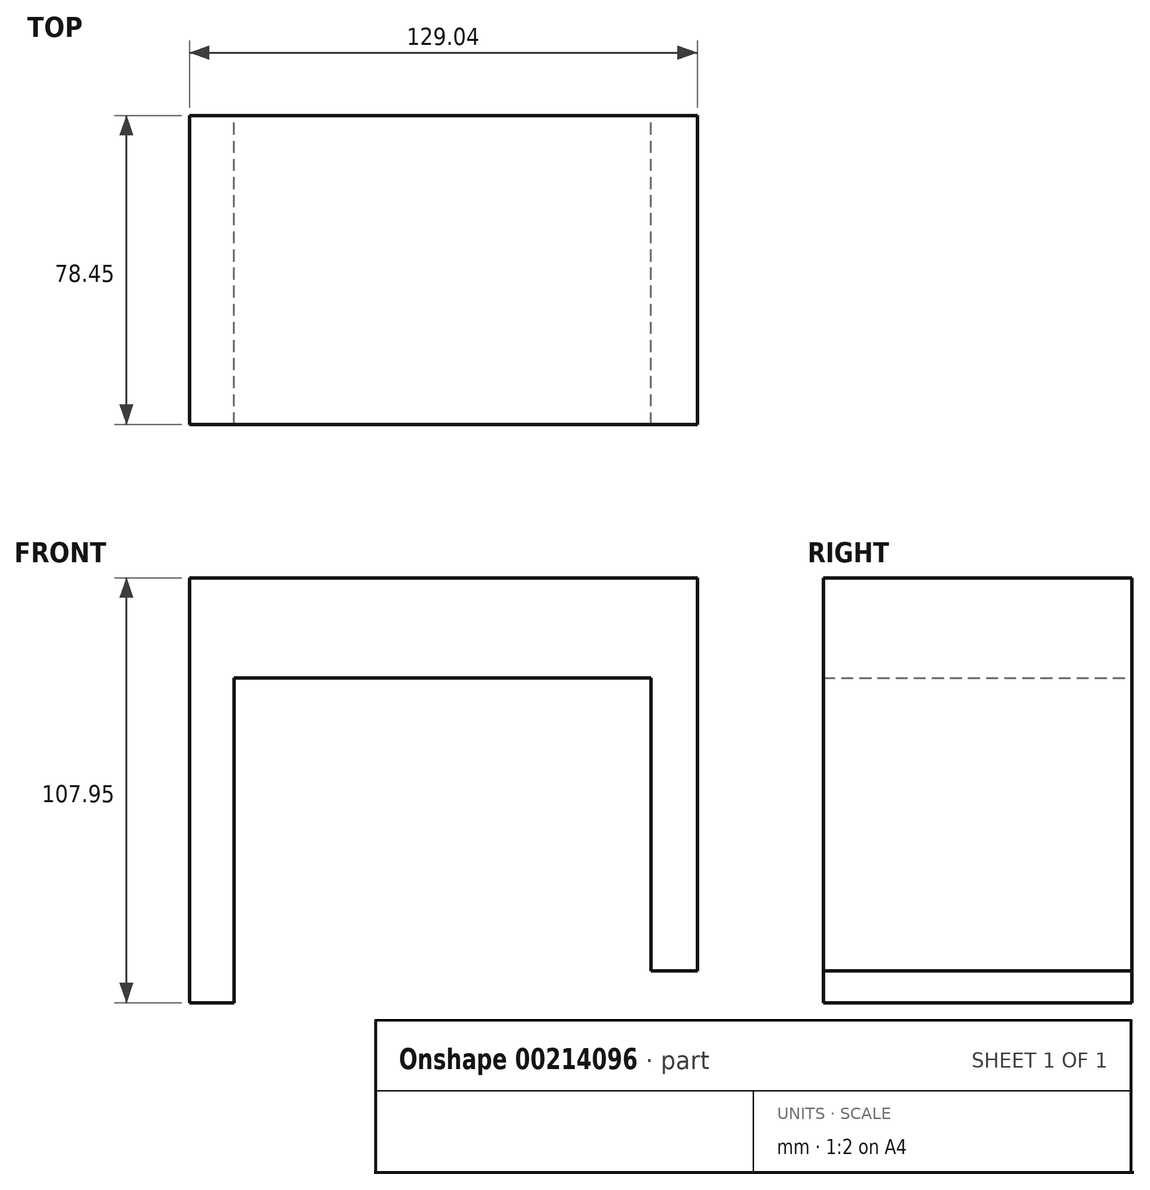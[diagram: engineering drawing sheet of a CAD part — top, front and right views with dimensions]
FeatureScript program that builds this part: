
annotation { "Feature Type Name" : "Feature", "Feature Type Description" : "" }
export const myFeature = defineFeature(function(context is Context, id is Id, definition is map)
    precondition{}
    {
        {
            var Q0;
            Q0=qCreatedBy(makeId("Top.planeOp"),FACE);
            var sketch = newSketch(context, id + "F0", { "sketchPlane" : qUnion([Q0])});
            skLineSegment(sketch, "E0.bottom", {"start": v(-67.82, 44.45) * mm, "end": v(61.22, 44.45) * mm});
            skLineSegment(sketch, "E0.top", {"start": v(-67.82, -34) * mm, "end": v(61.22, -34) * mm});
            skLineSegment(sketch, "E0.left", {"start": v(-67.82, 44.45) * mm, "end": v(-67.82, -34) * mm});
            skLineSegment(sketch, "E0.right", {"start": v(61.22, 44.45) * mm, "end": v(61.22, -34) * mm});
            skSolve(sketch);
        }
        {
            var Q0;
            Q0=makeQuery(id+"F0.imprint","IMPRINT",FACE,{"disambiguationData":[TD([[makeQuery(id+"F0.imprint","IMPRINT",EDGE,{"derivedFrom":sQuery(id+"F0.wireOp",EDGE,"E0.bottom")}),-1.0]])]});
            extrude(context, id + "F1", {"entities" : qUnion([Q0]), "depth" : 25.4 * mm});
        }
        {
            var Q0;
            Q0=makeQuery(id+"F1.opExtrude","CAP_FACE",FACE,{"disambiguationData":[OSD([sQuery(id+"F0.wireOp",EDGE,"E0.bottom"),sQuery(id+"F0.wireOp",EDGE,"E0.top"),sQuery(id+"F0.wireOp",EDGE,"E0.left"),sQuery(id+"F0.wireOp",EDGE,"E0.right")])],"isStart":true});
            var sketch = newSketch(context, id + "F2", { "sketchPlane" : qUnion([Q0])});
            skLineSegment(sketch, "E1.bottom", {"start": v(-67.82, 34) * mm, "end": v(-56.5, 34) * mm});
            skLineSegment(sketch, "E1.top", {"start": v(-67.82, -44.45) * mm, "end": v(-56.5, -44.45) * mm});
            skLineSegment(sketch, "E1.left", {"start": v(-67.82, 34) * mm, "end": v(-67.82, -44.45) * mm});
            skLineSegment(sketch, "E1.right", {"start": v(-56.5, 34) * mm, "end": v(-56.5, -44.45) * mm});
            skSolve(sketch);
        }
        {
            var Q0;
            Q0=makeQuery(id+"F2.imprint","IMPRINT",FACE,{"disambiguationData":[TD([[makeQuery(id+"F2.imprint","IMPRINT",EDGE,{"derivedFrom":sQuery(id+"F2.wireOp",EDGE,"E1.bottom")}),-1.0]])]});
            extrude(context, id + "F3", {"entities" : qUnion([Q0]), "operationType" : NewBodyOperationType.ADD, "depth" : 82.55 * mm});
        }
        {
            var Q0;
            Q0=makeQuery(id+"F1.opExtrude","CAP_FACE",FACE,{"disambiguationData":[OSD([sQuery(id+"F0.wireOp",EDGE,"E0.bottom"),sQuery(id+"F0.wireOp",EDGE,"E0.top"),sQuery(id+"F0.wireOp",EDGE,"E0.left"),sQuery(id+"F0.wireOp",EDGE,"E0.right")])],"isStart":true});
            var sketch = newSketch(context, id + "F4", { "sketchPlane" : qUnion([Q0])});
            skLineSegment(sketch, "E2.bottom", {"start": v(61.22, 34) * mm, "end": v(49.47, 34) * mm});
            skLineSegment(sketch, "E2.top", {"start": v(61.22, -44.45) * mm, "end": v(49.47, -44.45) * mm});
            skLineSegment(sketch, "E2.left", {"start": v(61.22, 34) * mm, "end": v(61.22, -44.45) * mm});
            skLineSegment(sketch, "E2.right", {"start": v(49.47, 34) * mm, "end": v(49.47, -44.45) * mm});
            skSolve(sketch);
        }
        {
            var Q0;
            Q0=makeQuery(id+"F4.imprint","IMPRINT",FACE,{"disambiguationData":[TD([[makeQuery(id+"F4.imprint","IMPRINT",EDGE,{"derivedFrom":sQuery(id+"F4.wireOp",EDGE,"E2.bottom")}),-1.0]])]});
            extrude(context, id + "F5", {"entities" : qUnion([Q0]), "operationType" : NewBodyOperationType.ADD, "depth" : 74.42 * mm});
        }
    });
